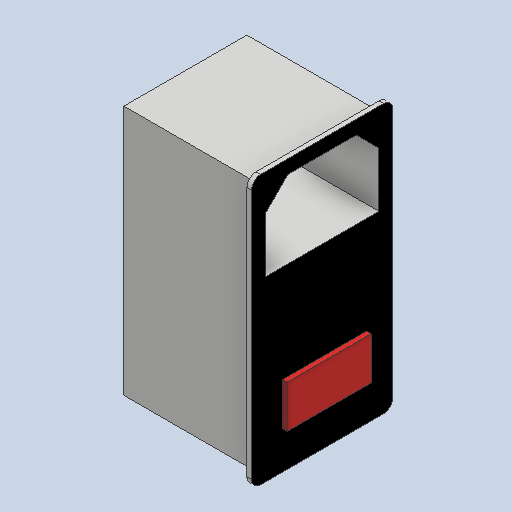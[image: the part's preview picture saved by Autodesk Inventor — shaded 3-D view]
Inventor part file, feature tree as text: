
AUTODESK INVENTOR PART (.ipt)
format: ipt  version: 2023 (Build 270158000, 158)  size: 147,968 bytes
history: native  units: mm
features: extrude x4, sketch x4, fillet x1
ambient origin geometry x8: Origin, YZ Plane, XZ Plane, XY Plane, X Axis, Y Axis, Z Axis, Center Point
bodies: Solid1 (feature_tree)
feature tree (9):
  extrude  "Extrusion1"  Depth=55.0mm
  extrude  "Extrusion2"  Depth=2.0mm
  fillet  "Fillet1"  Radius=2.0mm
  extrude  "Extrusion3"  Depth=2.0mm
  extrude  "Extrusion4"  Depth=2.0mm
  sketch  "Sketch1"  dims[d0=27.0mm d1=55.0mm]
  sketch  "Sketch2"  dims[d2=30.0mm d3=0.0mm d4=2.0mm d5=2.0mm]
  sketch  "Sketch3"  dims[d6=2.0mm d7=2.0mm]
  sketch  "Sketch4"  dims[d8=1.0mm d9=0.0mm d10=2.0mm d11=17.0mm d12=25.0mm d13=31.0mm d14=3.0mm d15=3.0mm d16=5.0mm d17=5.0mm d18=5.0mm d19=5.0mm d20=20.0mm d21=0.0mm d22=1.0mm d23=0.0mm]
